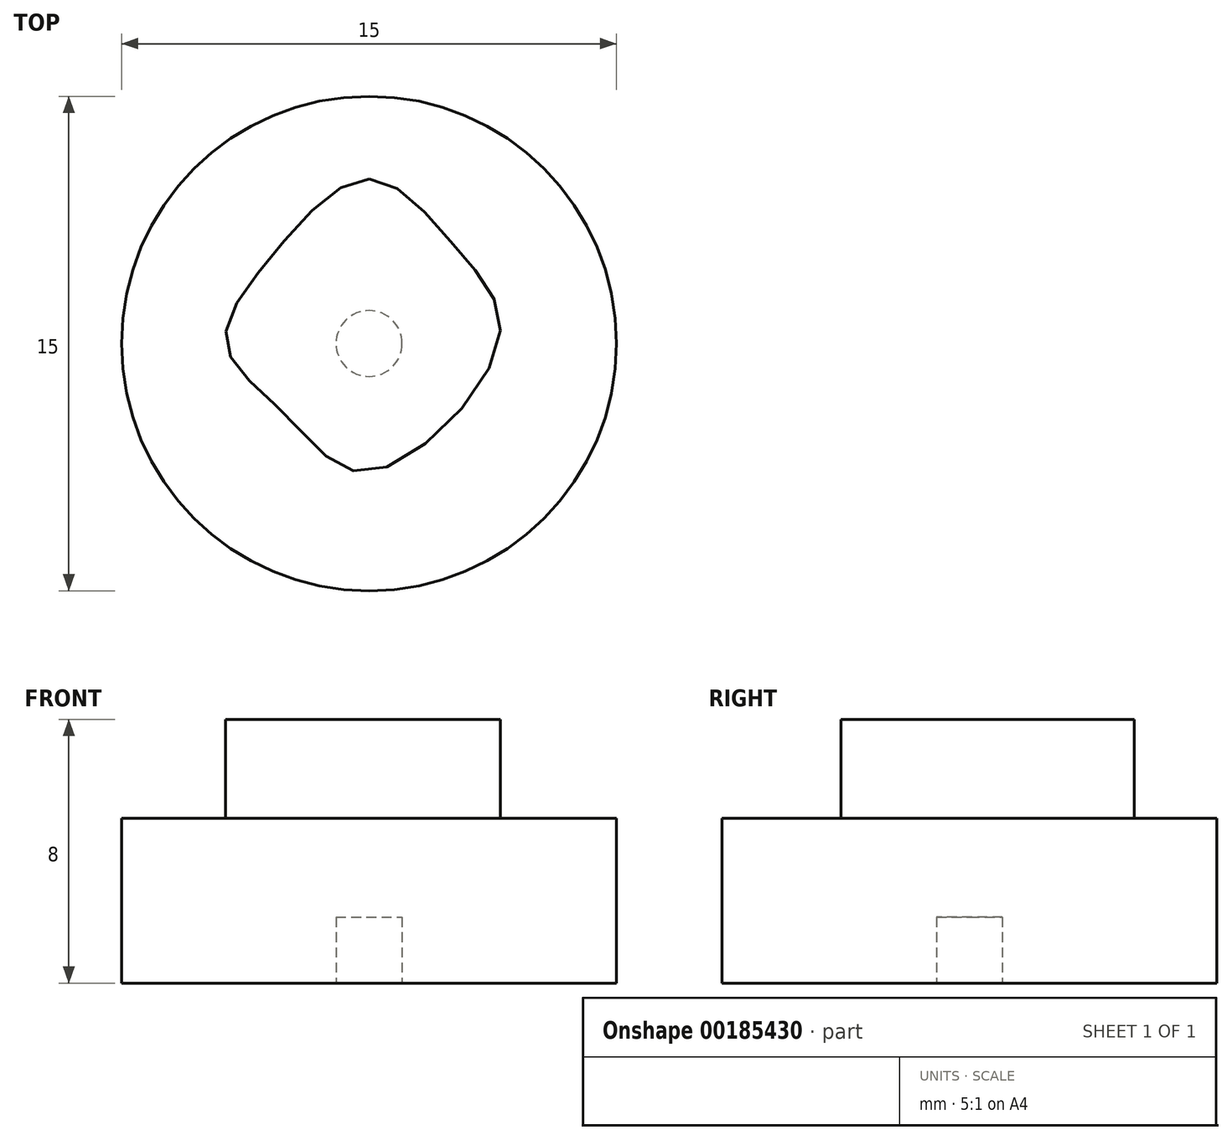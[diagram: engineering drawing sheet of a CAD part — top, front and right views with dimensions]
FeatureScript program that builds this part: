
annotation { "Feature Type Name" : "Feature", "Feature Type Description" : "" }
export const myFeature = defineFeature(function(context is Context, id is Id, definition is map)
    precondition{}
    {
        {
            var Q0;
            Q0=qCreatedBy(makeId("Top.planeOp"),FACE);
            var sketch = newSketch(context, id + "F0", { "sketchPlane" : qUnion([Q0])});
            skCircle(sketch, "E0", {"center": v(0, 0) * mm, "radius": 7.5 * mm});
            skSolve(sketch);
        }
        {
            var Q0;
            Q0 = qSketchRegion(id + "F0", true);
            extrude(context, id + "F1", {"entities" : qUnion([Q0]), "depth" : 5 * mm});
        }
        {
            var Q0;
            Q0=makeQuery(id+"F1.opExtrude","CAP_FACE",FACE,{"disambiguationData":[OSD([sQuery(id+"F0.wireOp",EDGE,"E0")])],"isStart":false});
            var sketch = newSketch(context, id + "F2", { "sketchPlane" : qUnion([Q0])});
            skFitSpline(sketch, "E1", {"points": [v(0, 5) * mm, v(-2.84, 2.79) * mm, v(-4.34, 0) * mm, v(-2.47, -2.22) * mm, v(0, -3.89) * mm, v(3.92, 0) * mm, v(2.66, 2.88) * mm, v(0, 5) * mm]});
            skSolve(sketch);
        }
        {
            var Q0;
            Q0 = qSketchRegion(id + "F2", true);
            extrude(context, id + "F3", {"entities" : qUnion([Q0]), "operationType" : NewBodyOperationType.ADD, "depth" : 3 * mm});
        }
        {
            var Q0;
            Q0=makeQuery(id+"F1.opExtrude","CAP_FACE",FACE,{"disambiguationData":[OSD([sQuery(id+"F0.wireOp",EDGE,"E0")])],"isStart":true});
            var sketch = newSketch(context, id + "F4", { "sketchPlane" : qUnion([Q0])});
            skCircle(sketch, "E2", {"center": v(0, 0) * mm, "radius": 1 * mm});
            skSolve(sketch);
        }
        {
            var Q0;
            Q0 = qSketchRegion(id + "F4", true);
            extrude(context, id + "F5", {"entities" : qUnion([Q0]), "operationType" : NewBodyOperationType.REMOVE, "oppositeDirection" : true, "depth" : 2 * mm});
        }
        {
            var Q0;
            Q0 = qSketchRegion(id + "F2", true);
            extrude(context, id + "F6", {"entities" : qUnion([Q0]), "operationType" : NewBodyOperationType.ADD, "depth" : 2 * mm});
        }
    });
